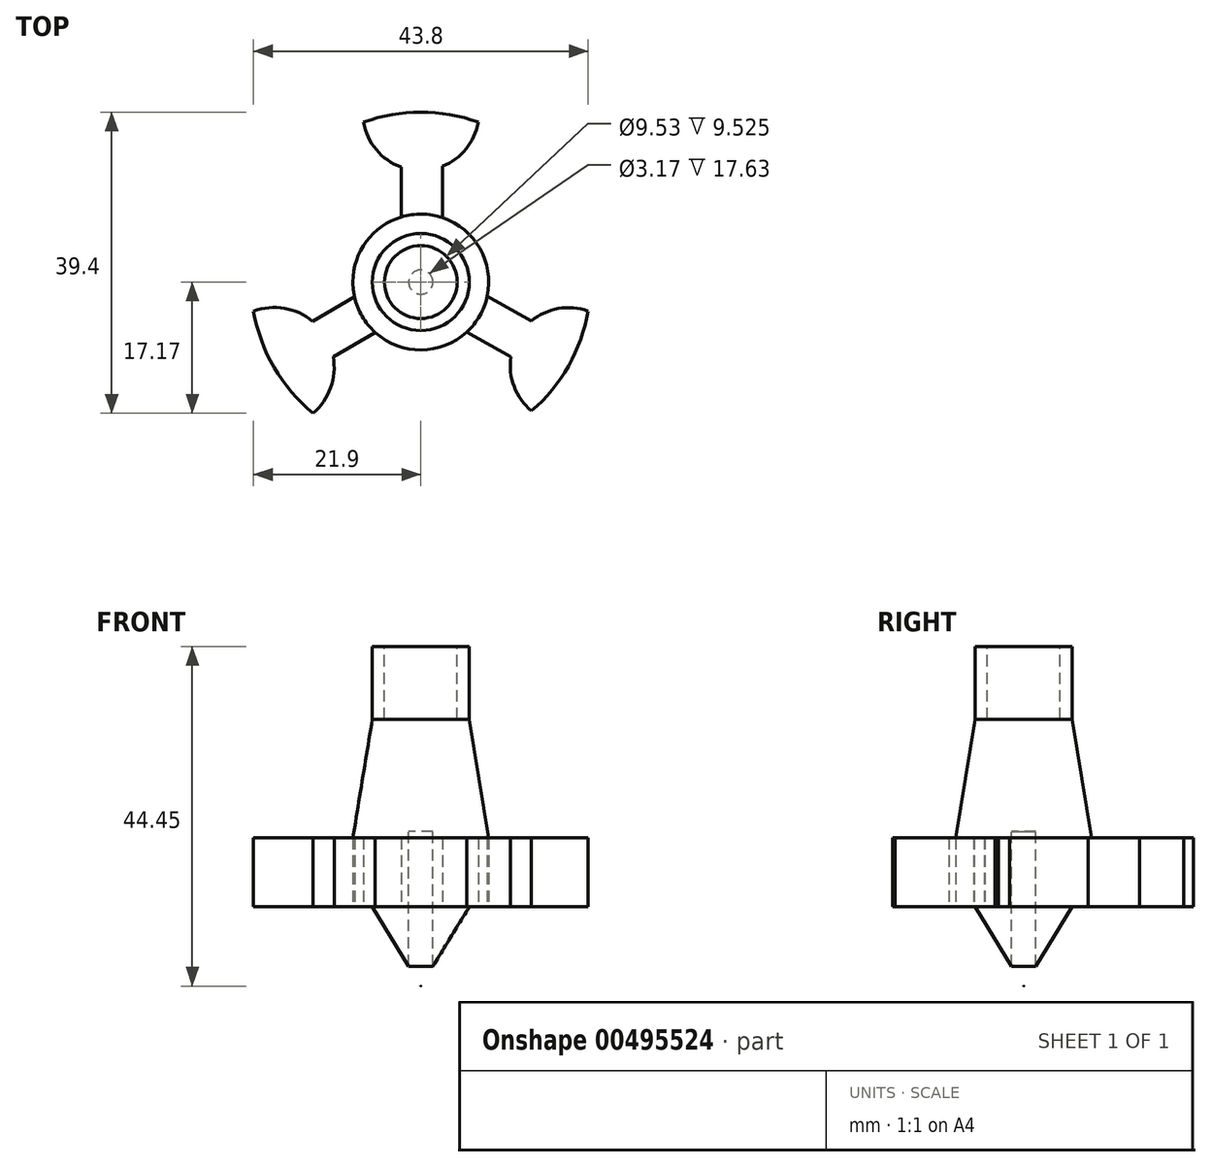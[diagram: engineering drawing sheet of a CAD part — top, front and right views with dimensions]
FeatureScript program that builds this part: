
annotation { "Feature Type Name" : "Feature", "Feature Type Description" : "" }
export const myFeature = defineFeature(function(context is Context, id is Id, definition is map)
    precondition{}
    {
        {
            var Q0;
            Q0=qCreatedBy(makeId("Front.planeOp"),FACE);
            var sketch = newSketch(context, id + "F0", { "sketchPlane" : qUnion([Q0])});
            skLineSegment(sketch, "E0", {"start": v(6.35, 34.05) * mm, "end": v(6.35, 24.53) * mm});
            skLineSegment(sketch, "E1", {"start": v(6.35, 0) * mm, "end": v(0, -10.4) * mm});
            skLineSegment(sketch, "E2.MirrorCS", {"start": v(-6.35, 0) * mm, "end": v(0, -10.4) * mm});
            skLineSegment(sketch, "E3.MirrorCS", {"start": v(-6.35, 34.05) * mm, "end": v(-6.35, 24.53) * mm});
            skLineSegment(sketch, "E4", {"start": v(6.35, 0) * mm, "end": v(22.23, 0) * mm});
            skLineSegment(sketch, "E5", {"start": v(22.23, 0) * mm, "end": v(22.23, 9.01) * mm});
            skLineSegment(sketch, "E6", {"start": v(22.23, 9.01) * mm, "end": v(8.89, 9.01) * mm});
            skLineSegment(sketch, "E7.MirrorCS", {"start": v(-22.23, 9.01) * mm, "end": v(-8.9, 9.01) * mm});
            skLineSegment(sketch, "E8.MirrorCS", {"start": v(-22.23, 0) * mm, "end": v(-22.23, 9.01) * mm});
            skLineSegment(sketch, "E9.MirrorCS", {"start": v(-6.35, 0) * mm, "end": v(-22.23, 0) * mm});
            skLineSegment(sketch, "E10", {"start": v(6.35, 24.53) * mm, "end": v(8.89, 9.01) * mm});
            skLineSegment(sketch, "E11", {"start": v(-6.35, 24.53) * mm, "end": v(-8.9, 9.01) * mm});
            skLineSegment(sketch, "E12", {"start": v(-6.35, 34.05) * mm, "end": v(6.35, 34.05) * mm});
            skLineSegment(sketch, "E13", {"start": v(0, -10.4) * mm, "end": v(0, 34.05) * mm});
            skSolve(sketch);
        }
        {
            var Q0;
            {var subQ0=sQuery(id+"F0.wireOp",EDGE,"E0");Q0=makeQuery(id+"F0.imprint","IMPRINT",FACE,{"disambiguationData":[TD([[makeQuery(id+"F0.imprint","IMPRINT",EDGE,{"derivedFrom":subQ0}),-1.0]])]});}
            var Q1;
            Q1=sQuery(id+"F0.wireOp",EDGE,"E13");
            revolve(context, id + "F1", {"entities" : qUnion([Q0]), "axis" : qUnion([Q1]), "revolveType" : RevolveType.FULL});
        }
        {
            var Q0;
            Q0=qCreatedBy(makeId("Top.planeOp"),FACE);
            var sketch = newSketch(context, id + "F2", { "sketchPlane" : qUnion([Q0])});
            skCircle(sketch, "E14", {"center": v(0, 0) * mm, "radius": 22.23 * mm});
            skArc(sketch, "E15", {"start": v(-7.5, 20.92) * mm, "mid": v(-5.82, 17.31) * mm, "end": v(-2.55, 15.05) * mm});
            skCircle(sketch, "E16", {"center": v(0, 0) * mm, "radius": 8.9 * mm});
            skPoint(sketch, "E17.orphan", {"position": v(0.8, -0.05) * mm});
            skArc(sketch, "E18.trimOffspring", {"start": v(2.83, 15.15) * mm, "mid": v(5.92, 17.42) * mm, "end": v(7.5, 20.92) * mm});
            skArc(sketch, "E19", {"start": v(-14.11, -17.17) * mm, "mid": v(-11.8, -13.83) * mm, "end": v(-11.47, -9.8) * mm});
            skArc(sketch, "E20", {"start": v(21.9, -3.8) * mm, "mid": v(18, -3.47) * mm, "end": v(14.46, -5.11) * mm});
            skLineSegment(sketch, "E21", {"start": v(-2.55, 15.05) * mm, "end": v(-2.55, 8.52) * mm});
            skLineSegment(sketch, "E22", {"start": v(2.83, 15.15) * mm, "end": v(2.83, 8.43) * mm});
            skLineSegment(sketch, "E23.trimOffspring", {"start": v(-11.47, -9.8) * mm, "end": v(-5.97, -6.59) * mm});
            skLineSegment(sketch, "E24.trimOffspring", {"start": v(-14.18, -5.14) * mm, "end": v(-8.68, -1.94) * mm});
            skLineSegment(sketch, "E25", {"start": v(11.8, -9.8) * mm, "end": v(6.04, -6.52) * mm});
            skLineSegment(sketch, "E26.MirrorCS", {"start": v(14.46, -5.11) * mm, "end": v(8.7, -1.84) * mm});
            skArc(sketch, "E27.trimOffspring", {"start": v(11.8, -9.8) * mm, "mid": v(12.2, -13.68) * mm, "end": v(14.49, -16.85) * mm});
            skArc(sketch, "E28.trimOffspring", {"start": v(-14.18, -5.14) * mm, "mid": v(-17.86, -3.44) * mm, "end": v(-21.9, -3.8) * mm});
            skSolve(sketch);
        }
        {
            var Q0;
            {var subQ0=sQuery(id+"F2.wireOp",EDGE,"E19");Q0=makeQuery(id+"F2.imprint","IMPRINT",FACE,{"disambiguationData":[TD([[makeQuery(id+"F2.imprint","IMPRINT",EDGE,{"derivedFrom":subQ0}),-1.0]])]});}
            var Q1;
            {var subQ0=sQuery(id+"F2.wireOp",EDGE,"E18.trimOffspring");Q1=makeQuery(id+"F2.imprint","IMPRINT",FACE,{"disambiguationData":[TD([[makeQuery(id+"F2.imprint","IMPRINT",EDGE,{"derivedFrom":subQ0}),-1.0]])]});}
            var Q2;
            {var subQ3=sQuery(id+"F2.wireOp",EDGE,"E15");Q2=makeQuery(id+"F2.imprint","IMPRINT",FACE,{"disambiguationData":[TD([[makeQuery(id+"F2.imprint","IMPRINT",EDGE,{"derivedFrom":subQ3}),-1.0]])]});}
            extrude(context, id + "F3", {"entities" : qUnion([Q0, Q1, Q2]), "operationType" : NewBodyOperationType.REMOVE, "depth" : 14.1 * mm});
        }
        {
            var Q0;
            Q0=makeQuery(id+"F1.opRevolve","SWEPT_FACE",FACE,{"disambiguationData":[OSD([sQuery(id+"F0.wireOp",EDGE,"E12")])]});
            var sketch = newSketch(context, id + "F4", { "sketchPlane" : qUnion([Q0])});
            skCircle(sketch, "E29", {"center": v(0, 0) * mm, "radius": 4.76 * mm});
            skSolve(sketch);
        }
        {
            var Q0;
            Q0=makeQuery(id+"F4.imprint","IMPRINT",FACE,{"disambiguationData":[TD([[makeQuery(id+"F4.imprint","IMPRINT",EDGE,{"derivedFrom":sQuery(id+"F4.wireOp",EDGE,"E29")}),1.0]])]});
            extrude(context, id + "F5", {"entities" : qUnion([Q0]), "operationType" : NewBodyOperationType.REMOVE, "oppositeDirection" : true, "depth" : 9.52 * mm});
        }
        {
            var Q0;
            Q0=qCreatedBy(makeId("Top.planeOp"),FACE);
            var sketch = newSketch(context, id + "F6", { "sketchPlane" : qUnion([Q0])});
            skCircle(sketch, "E30", {"center": v(0, 0) * mm, "radius": 1.59 * mm});
            skSolve(sketch);
        }
        {
            var Q0;
            Q0=qSketchRegion(id+"F6",true);
            extrude(context, id + "F7", {"entities" : qUnion([Q0]), "operationType" : NewBodyOperationType.REMOVE, "oppositeDirection" : true, "depth" : 10.4 * mm});
        }
        {
            var Q0;
            Q0=qCreatedBy(makeId("Top.planeOp"),FACE);
            var sketch = newSketch(context, id + "F8", { "sketchPlane" : qUnion([Q0])});
            skCircle(sketch, "E31", {"center": v(0, 0) * mm, "radius": 1.59 * mm});
            skSolve(sketch);
        }
        {
            var Q0;
            Q0=makeQuery(id+"F8.imprint","IMPRINT",FACE,{"disambiguationData":[TD([[makeQuery(id+"F8.imprint","IMPRINT",EDGE,{"derivedFrom":sQuery(id+"F8.wireOp",EDGE,"E31")}),1.0]])]});
            extrude(context, id + "F9", {"entities" : qUnion([Q0]), "operationType" : NewBodyOperationType.REMOVE, "depth" : 9.83 * mm});
        }
    });
